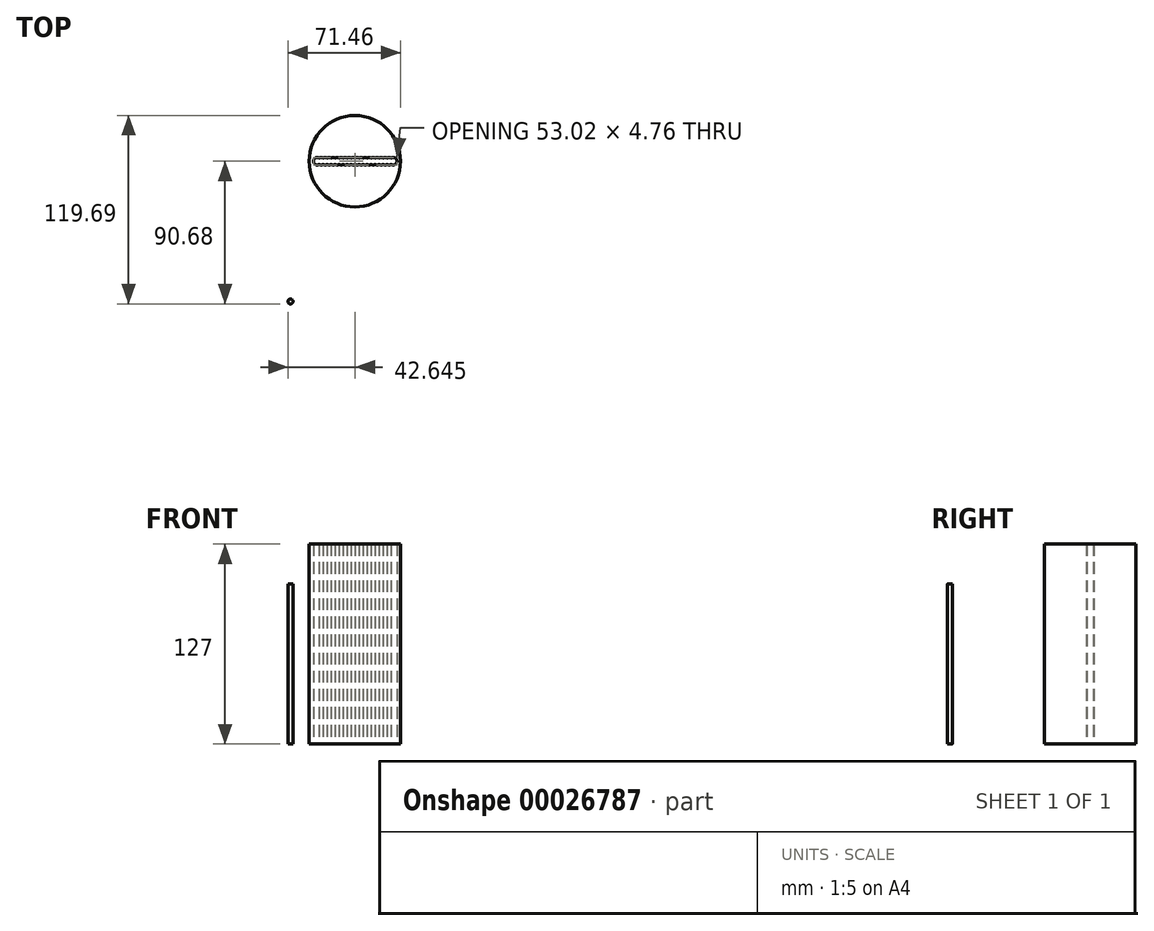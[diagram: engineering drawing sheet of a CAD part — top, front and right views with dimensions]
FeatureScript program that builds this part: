
annotation { "Feature Type Name" : "Feature", "Feature Type Description" : "" }
export const myFeature = defineFeature(function(context is Context, id is Id, definition is map)
    precondition{}
    {
        {
            var Q0;
            Q0=qCreatedBy(makeId("Top.planeOp"),FACE);
            var sketch = newSketch(context, id + "F0", { "sketchPlane" : qUnion([Q0])});
            skCircle(sketch, "E0", {"center": v(0, 0) * mm, "radius": 29 * mm});
            skCircle(sketch, "E1", {"center": v(-23.93, 0) * mm, "radius": 2.38 * mm});
            skCircle(sketch, "E2.1.0.0", {"center": v(-21.4, 0) * mm, "radius": 2.38 * mm});
            skCircle(sketch, "E2.2.0.0", {"center": v(-18.85, 0) * mm, "radius": 2.38 * mm});
            skCircle(sketch, "E2.3.0.0", {"center": v(-16.31, 0) * mm, "radius": 2.38 * mm});
            skCircle(sketch, "E2.4.0.0", {"center": v(-13.77, 0) * mm, "radius": 2.38 * mm});
            skCircle(sketch, "E2.5.0.0", {"center": v(-11.23, 0) * mm, "radius": 2.38 * mm});
            skCircle(sketch, "E2.6.0.0", {"center": v(-8.7, 0) * mm, "radius": 2.38 * mm});
            skCircle(sketch, "E2.7.0.0", {"center": v(-6.15, 0) * mm, "radius": 2.38 * mm});
            skCircle(sketch, "E2.8.0.0", {"center": v(-3.61, 0) * mm, "radius": 2.38 * mm});
            skCircle(sketch, "E2.9.0.0", {"center": v(-1.07, 0) * mm, "radius": 2.38 * mm});
            skCircle(sketch, "E2.10.0.0", {"center": v(1.47, 0) * mm, "radius": 2.38 * mm});
            skCircle(sketch, "E2.11.0.0", {"center": v(4, 0) * mm, "radius": 2.38 * mm});
            skCircle(sketch, "E2.12.0.0", {"center": v(6.55, 0) * mm, "radius": 2.38 * mm});
            skCircle(sketch, "E2.13.0.0", {"center": v(9.09, 0) * mm, "radius": 2.38 * mm});
            skCircle(sketch, "E2.14.0.0", {"center": v(11.63, 0) * mm, "radius": 2.38 * mm});
            skCircle(sketch, "E2.15.0.0", {"center": v(14.17, 0) * mm, "radius": 2.38 * mm});
            skCircle(sketch, "E2.16.0.0", {"center": v(16.7, 0) * mm, "radius": 2.38 * mm});
            skCircle(sketch, "E2.17.0.0", {"center": v(19.25, 0) * mm, "radius": 2.38 * mm});
            skCircle(sketch, "E2.18.0.0", {"center": v(21.79, 0) * mm, "radius": 2.38 * mm});
            skCircle(sketch, "E2.19.0.0", {"center": v(24.33, 0) * mm, "radius": 2.38 * mm});
            skLineSegment(sketch, "E2.direction1", {"start": v(-23.93, 0) * mm, "end": v(-21.4, 0) * mm, "construction": true});
            skSolve(sketch);
        }
        {
            var Q0;
            Q0=makeQuery(id+"F0.imprint","IMPRINT",FACE,{"disambiguationData":[TD([[makeQuery(id+"F0.imprint","IMPRINT",EDGE,{"derivedFrom":sQuery(id+"F0.wireOp",EDGE,"E0")}),1.0]])]});
            extrude(context, id + "F1", {"entities" : qUnion([Q0]), "depth" : 127 * mm});
        }
        {
            var Q0;
            Q0=qCreatedBy(makeId("Top.planeOp"),FACE);
            var sketch = newSketch(context, id + "F2", { "sketchPlane" : qUnion([Q0])});
            skCircle(sketch, "E3", {"center": v(-40.88, -89.11) * mm, "radius": 1.57 * mm});
            skSolve(sketch);
        }
        {
            var Q0;
            Q0=makeQuery(id+"F2.imprint","IMPRINT",FACE,{"disambiguationData":[TD([[makeQuery(id+"F2.imprint","IMPRINT",EDGE,{"derivedFrom":sQuery(id+"F2.wireOp",EDGE,"E3")}),1.0]])]});
            extrude(context, id + "F3", {"entities" : qUnion([Q0]), "depth" : 101.6 * mm});
        }
    });
